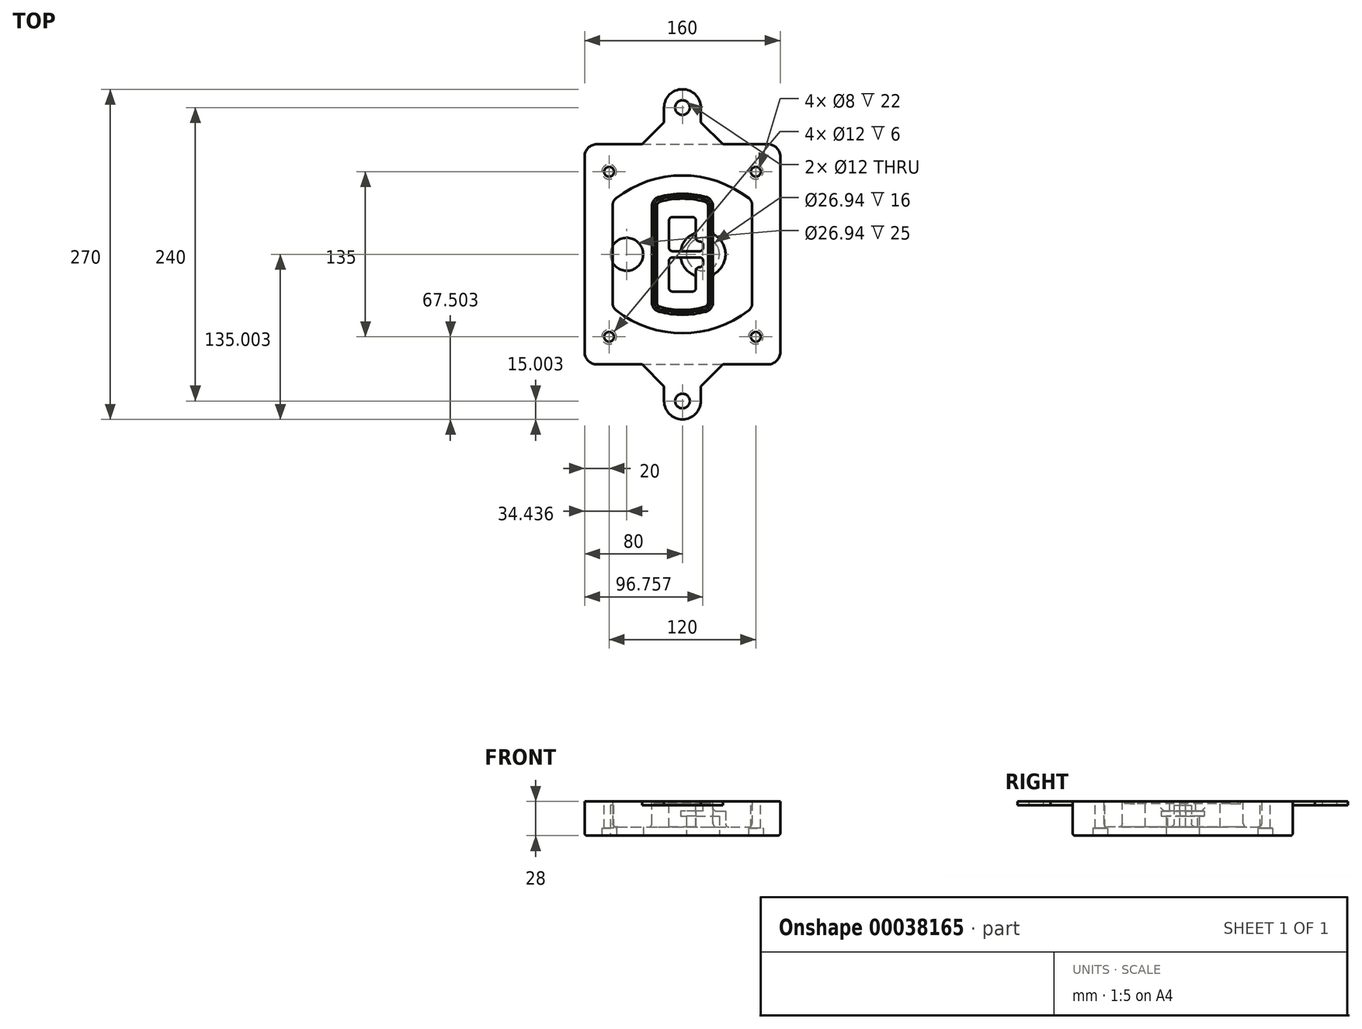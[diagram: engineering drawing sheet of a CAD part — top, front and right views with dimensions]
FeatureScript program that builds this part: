
annotation { "Feature Type Name" : "Feature", "Feature Type Description" : "" }
export const myFeature = defineFeature(function(context is Context, id is Id, definition is map)
    precondition{}
    {
        {
            var Q0;
            Q0=qCreatedBy(makeId("Top.planeOp"),FACE);
            var sketch = newSketch(context, id + "F0", { "sketchPlane" : qUnion([Q0])});
            skPoint(sketch, "E0.rect.middle", {"position": v(0, 0) * mm});
            skLineSegment(sketch, "E1.bottom", {"start": v(24.05, 28.38) * mm, "end": v(164.05, 28.38) * mm});
            skLineSegment(sketch, "E1.top", {"start": v(24.05, 208.38) * mm, "end": v(164.05, 208.38) * mm});
            skLineSegment(sketch, "E1.left", {"start": v(14.05, 38.38) * mm, "end": v(14.05, 198.38) * mm});
            skLineSegment(sketch, "E1.right", {"start": v(174.05, 38.38) * mm, "end": v(174.05, 198.38) * mm});
            skLineSegment(sketch, "E2", {"start": v(14.05, 208.38) * mm, "end": v(174.05, 28.38) * mm, "construction": true});
            skLineSegment(sketch, "E3", {"start": v(174.05, 208.38) * mm, "end": v(14.05, 28.38) * mm, "construction": true});
            skCircle(sketch, "E4", {"center": v(34.05, 185.88) * mm, "radius": 4 * mm});
            skCircle(sketch, "E5", {"center": v(154.05, 185.88) * mm, "radius": 4 * mm});
            skCircle(sketch, "E6", {"center": v(154.05, 50.88) * mm, "radius": 4 * mm});
            skCircle(sketch, "E7", {"center": v(34.05, 50.88) * mm, "radius": 4 * mm});
            skLineSegment(sketch, "E8", {"start": v(34.05, 185.88) * mm, "end": v(154.05, 185.88) * mm, "construction": true});
            skLineSegment(sketch, "E9", {"start": v(154.05, 185.88) * mm, "end": v(154.05, 50.88) * mm, "construction": true});
            skLineSegment(sketch, "E10", {"start": v(154.05, 50.88) * mm, "end": v(34.05, 50.88) * mm, "construction": true});
            skLineSegment(sketch, "E11", {"start": v(34.05, 50.88) * mm, "end": v(34.05, 185.88) * mm, "construction": true});
            skLineSegment(sketch, "E12", {"start": v(34.05, 158.68) * mm, "end": v(34.05, 78.09) * mm});
            skLineSegment(sketch, "E13", {"start": v(154.05, 158.68) * mm, "end": v(154.05, 78.09) * mm});
            skArc(sketch, "E14", {"start": v(150.2, 166.56) * mm, "mid": v(94.05, 185.88) * mm, "end": v(37.9, 166.56) * mm});
            skArc(sketch, "E15", {"start": v(37.9, 70.2) * mm, "mid": v(94.05, 50.88) * mm, "end": v(150.2, 70.2) * mm});
            skLineSegment(sketch, "E16", {"start": v(34.05, 118.38) * mm, "end": v(154.05, 118.38) * mm, "construction": true});
            skPoint(sketch, "E17.visualSharp", {"position": v(34.05, 73.38) * mm});
            skArc(sketch, "E17.filletArc", {"start": v(34.05, 78.09) * mm, "mid": v(35.06, 73.7) * mm, "end": v(37.9, 70.2) * mm});
            skPoint(sketch, "E18.visualSharp", {"position": v(34.05, 163.38) * mm});
            skArc(sketch, "E18.filletArc", {"start": v(37.9, 166.56) * mm, "mid": v(35.06, 163.06) * mm, "end": v(34.05, 158.68) * mm});
            skPoint(sketch, "E19.visualSharp", {"position": v(154.05, 163.38) * mm});
            skArc(sketch, "E19.filletArc", {"start": v(154.05, 158.68) * mm, "mid": v(153.04, 163.06) * mm, "end": v(150.2, 166.56) * mm});
            skPoint(sketch, "E20.visualSharp", {"position": v(154.05, 73.38) * mm});
            skArc(sketch, "E20.filletArc", {"start": v(150.2, 70.2) * mm, "mid": v(153.04, 73.7) * mm, "end": v(154.05, 78.09) * mm});
            skPoint(sketch, "E21.visualSharp", {"position": v(14.05, 208.38) * mm});
            skArc(sketch, "E21.filletArc", {"start": v(24.05, 208.38) * mm, "mid": v(16.98, 205.45) * mm, "end": v(14.05, 198.38) * mm});
            skPoint(sketch, "E22.visualSharp", {"position": v(174.05, 208.38) * mm});
            skArc(sketch, "E22.filletArc", {"start": v(174.05, 198.38) * mm, "mid": v(171.12, 205.45) * mm, "end": v(164.05, 208.38) * mm});
            skPoint(sketch, "E23.visualSharp", {"position": v(174.05, 28.38) * mm});
            skArc(sketch, "E23.filletArc", {"start": v(164.05, 28.38) * mm, "mid": v(171.12, 31.31) * mm, "end": v(174.05, 38.38) * mm});
            skPoint(sketch, "E24.visualSharp", {"position": v(14.05, 28.38) * mm});
            skArc(sketch, "E24.filletArc", {"start": v(14.05, 38.38) * mm, "mid": v(16.98, 31.31) * mm, "end": v(24.05, 28.38) * mm});
            skArc(sketch, "E25.0", {"start": v(151.05, 158.68) * mm, "mid": v(150.34, 161.75) * mm, "end": v(148.36, 164.2) * mm});
            skLineSegment(sketch, "E25.1", {"start": v(151.05, 158.68) * mm, "end": v(151.05, 78.09) * mm});
            skArc(sketch, "E25.2", {"start": v(148.36, 72.57) * mm, "mid": v(150.34, 75.02) * mm, "end": v(151.05, 78.09) * mm});
            skArc(sketch, "E25.3", {"start": v(39.74, 72.57) * mm, "mid": v(94.05, 53.88) * mm, "end": v(148.36, 72.57) * mm});
            skArc(sketch, "E25.4", {"start": v(37.05, 78.09) * mm, "mid": v(37.76, 75.02) * mm, "end": v(39.74, 72.57) * mm});
            skArc(sketch, "E25.5", {"start": v(148.36, 164.2) * mm, "mid": v(94.05, 182.88) * mm, "end": v(39.74, 164.2) * mm});
            skLineSegment(sketch, "E25.6", {"start": v(37.05, 158.68) * mm, "end": v(37.05, 78.09) * mm});
            skArc(sketch, "E25.7", {"start": v(39.74, 164.2) * mm, "mid": v(37.76, 161.75) * mm, "end": v(37.05, 158.68) * mm});
            skArc(sketch, "E26.0", {"start": v(35.43, 169.71) * mm, "mid": v(31.47, 164.82) * mm, "end": v(30.05, 158.68) * mm});
            skArc(sketch, "E26.1", {"start": v(152.67, 169.71) * mm, "mid": v(94.05, 189.88) * mm, "end": v(35.43, 169.71) * mm});
            skArc(sketch, "E26.2", {"start": v(158.05, 158.68) * mm, "mid": v(156.63, 164.82) * mm, "end": v(152.67, 169.71) * mm});
            skLineSegment(sketch, "E26.3", {"start": v(158.05, 158.68) * mm, "end": v(158.05, 78.09) * mm});
            skArc(sketch, "E26.4", {"start": v(152.67, 67.05) * mm, "mid": v(156.63, 71.95) * mm, "end": v(158.05, 78.09) * mm});
            skLineSegment(sketch, "E26.5", {"start": v(30.05, 158.68) * mm, "end": v(30.05, 78.09) * mm});
            skArc(sketch, "E26.6", {"start": v(35.43, 67.05) * mm, "mid": v(94.05, 46.88) * mm, "end": v(152.67, 67.05) * mm});
            skArc(sketch, "E26.7", {"start": v(30.05, 78.09) * mm, "mid": v(31.47, 71.95) * mm, "end": v(35.43, 67.05) * mm});
            skSolve(sketch);
        }
        {
            var Q0;
            Q0=makeQuery(id+"F0.imprint","IMPRINT",FACE,{"disambiguationData":[TD([[makeQuery(id+"F0.imprint","IMPRINT",EDGE,{"derivedFrom":sQuery(id+"F0.wireOp",EDGE,"E1.bottom")}),1.0]])]});
            var Q1;
            Q1=makeQuery(id+"F0.imprint","IMPRINT",FACE,{"disambiguationData":[TD([[makeQuery(id+"F0.imprint","IMPRINT",EDGE,{"derivedFrom":sQuery(id+"F0.wireOp",EDGE,"E12")}),1.0]])]});
            var Q2;
            Q2=makeQuery(id+"F0.imprint","IMPRINT",FACE,{"disambiguationData":[TD([[makeQuery(id+"F0.imprint","IMPRINT",EDGE,{"derivedFrom":sQuery(id+"F0.wireOp",EDGE,"E25.0")}),1.0]])]});
            var Q3;
            Q3=makeQuery(id+"F0.imprint","IMPRINT",FACE,{"disambiguationData":[TD([[makeQuery(id+"F0.imprint","IMPRINT",EDGE,{"derivedFrom":sQuery(id+"F0.wireOp",EDGE,"E12")}),-1.0]])]});
            extrude(context, id + "F1", {"entities" : qUnion([Q0, Q1, Q2, Q3]), "oppositeDirection" : true, "depth" : 25 * mm});
        }
        {
            var Q0;
            Q0=makeQuery(id+"F0.imprint","IMPRINT",FACE,{"disambiguationData":[TD([[makeQuery(id+"F0.imprint","IMPRINT",EDGE,{"derivedFrom":sQuery(id+"F0.wireOp",EDGE,"E12")}),1.0]])]});
            extrude(context, id + "F2", {"entities" : qUnion([Q0]), "operationType" : NewBodyOperationType.ADD, "depth" : 3 * mm});
        }
        {
            var Q0;
            Q0=makeQuery(id+"F0.imprint","IMPRINT",FACE,{"disambiguationData":[TD([[makeQuery(id+"F0.imprint","IMPRINT",EDGE,{"derivedFrom":sQuery(id+"F0.wireOp",EDGE,"E25.0")}),1.0]])]});
            extrude(context, id + "F3", {"entities" : qUnion([Q0]), "operationType" : NewBodyOperationType.REMOVE, "oppositeDirection" : true, "depth" : 18 * mm});
        }
        {
            var Q0;
            Q0=makeQuery(id+"F2.opExtrude","CAP_FACE",FACE,{"disambiguationData":[OSD([sQuery(id+"F0.wireOp",EDGE,"E12"),sQuery(id+"F0.wireOp",EDGE,"E13"),sQuery(id+"F0.wireOp",EDGE,"E14"),sQuery(id+"F0.wireOp",EDGE,"E15"),sQuery(id+"F0.wireOp",EDGE,"E17.filletArc"),sQuery(id+"F0.wireOp",EDGE,"E18.filletArc"),sQuery(id+"F0.wireOp",EDGE,"E19.filletArc"),sQuery(id+"F0.wireOp",EDGE,"E20.filletArc"),sQuery(id+"F0.wireOp",EDGE,"E25.0"),sQuery(id+"F0.wireOp",EDGE,"E25.1"),sQuery(id+"F0.wireOp",EDGE,"E25.2"),sQuery(id+"F0.wireOp",EDGE,"E25.3"),sQuery(id+"F0.wireOp",EDGE,"E25.4"),sQuery(id+"F0.wireOp",EDGE,"E25.5"),sQuery(id+"F0.wireOp",EDGE,"E25.6"),sQuery(id+"F0.wireOp",EDGE,"E25.7")])],"isStart":false});
            var sketch = newSketch(context, id + "F4", { "sketchPlane" : qUnion([Q0])});
            skArc(sketch, "E27.0", {"start": v(74.97, 71.41) * mm, "mid": v(94.05, 68.88) * mm, "end": v(113.13, 71.41) * mm});
            skArc(sketch, "E28.0", {"start": v(113.13, 165.35) * mm, "mid": v(94.05, 167.88) * mm, "end": v(74.97, 165.35) * mm});
            skLineSegment(sketch, "E29", {"start": v(69.05, 157.63) * mm, "end": v(69.05, 79.14) * mm});
            skLineSegment(sketch, "E30", {"start": v(119.05, 157.63) * mm, "end": v(119.05, 79.14) * mm});
            skLineSegment(sketch, "E31", {"start": v(69.05, 163.48) * mm, "end": v(119.05, 163.48) * mm, "construction": true});
            skLineSegment(sketch, "E32", {"start": v(69.05, 73.28) * mm, "end": v(119.05, 73.28) * mm, "construction": true});
            skPoint(sketch, "E33.visualSharp", {"position": v(69.05, 163.48) * mm});
            skArc(sketch, "E33.filletArc", {"start": v(74.97, 165.35) * mm, "mid": v(70.7, 162.5) * mm, "end": v(69.05, 157.63) * mm});
            skPoint(sketch, "E34.visualSharp", {"position": v(119.05, 163.48) * mm});
            skArc(sketch, "E34.filletArc", {"start": v(119.05, 157.63) * mm, "mid": v(117.4, 162.5) * mm, "end": v(113.13, 165.35) * mm});
            skPoint(sketch, "E35.visualSharp", {"position": v(119.05, 73.28) * mm});
            skArc(sketch, "E35.filletArc", {"start": v(113.13, 71.41) * mm, "mid": v(117.4, 74.27) * mm, "end": v(119.05, 79.14) * mm});
            skPoint(sketch, "E36.visualSharp", {"position": v(69.05, 73.28) * mm});
            skArc(sketch, "E36.filletArc", {"start": v(69.05, 79.14) * mm, "mid": v(70.7, 74.27) * mm, "end": v(74.97, 71.41) * mm});
            skArc(sketch, "E37.0", {"start": v(148.36, 164.2) * mm, "mid": v(94.05, 182.88) * mm, "end": v(39.74, 164.2) * mm});
            skArc(sketch, "E37.1", {"start": v(39.74, 164.2) * mm, "mid": v(37.76, 161.75) * mm, "end": v(37.05, 158.68) * mm});
            skLineSegment(sketch, "E37.2", {"start": v(37.05, 158.68) * mm, "end": v(37.05, 78.09) * mm});
            skArc(sketch, "E37.3", {"start": v(37.05, 78.09) * mm, "mid": v(37.76, 75.02) * mm, "end": v(39.74, 72.57) * mm});
            skArc(sketch, "E37.4", {"start": v(39.74, 72.57) * mm, "mid": v(94.05, 53.88) * mm, "end": v(148.36, 72.57) * mm});
            skArc(sketch, "E37.5", {"start": v(148.36, 72.57) * mm, "mid": v(150.34, 75.02) * mm, "end": v(151.05, 78.09) * mm});
            skLineSegment(sketch, "E37.6", {"start": v(151.05, 158.68) * mm, "end": v(151.05, 78.09) * mm});
            skArc(sketch, "E37.7", {"start": v(151.05, 158.68) * mm, "mid": v(150.34, 161.75) * mm, "end": v(148.36, 164.2) * mm});
            skLineSegment(sketch, "E38.0", {"start": v(117.05, 157.63) * mm, "end": v(117.05, 79.14) * mm});
            skArc(sketch, "E38.1", {"start": v(112.61, 73.34) * mm, "mid": v(115.81, 75.49) * mm, "end": v(117.05, 79.14) * mm});
            skArc(sketch, "E38.2", {"start": v(75.49, 73.34) * mm, "mid": v(94.05, 70.88) * mm, "end": v(112.61, 73.34) * mm});
            skArc(sketch, "E38.3", {"start": v(71.05, 79.14) * mm, "mid": v(72.29, 75.49) * mm, "end": v(75.49, 73.34) * mm});
            skLineSegment(sketch, "E38.4", {"start": v(71.05, 157.63) * mm, "end": v(71.05, 79.14) * mm});
            skArc(sketch, "E38.5", {"start": v(117.05, 157.63) * mm, "mid": v(115.81, 161.28) * mm, "end": v(112.61, 163.42) * mm});
            skArc(sketch, "E38.6", {"start": v(75.49, 163.42) * mm, "mid": v(72.29, 161.28) * mm, "end": v(71.05, 157.63) * mm});
            skArc(sketch, "E38.7", {"start": v(112.61, 163.42) * mm, "mid": v(94.05, 165.88) * mm, "end": v(75.49, 163.42) * mm});
            skArc(sketch, "E39.0", {"start": v(115.05, 157.63) * mm, "mid": v(114.23, 160.06) * mm, "end": v(112.1, 161.5) * mm});
            skLineSegment(sketch, "E39.1", {"start": v(115.05, 157.63) * mm, "end": v(115.05, 79.14) * mm});
            skArc(sketch, "E39.2", {"start": v(112.1, 75.27) * mm, "mid": v(114.23, 76.7) * mm, "end": v(115.05, 79.14) * mm});
            skArc(sketch, "E39.3", {"start": v(76, 75.27) * mm, "mid": v(94.05, 72.88) * mm, "end": v(112.1, 75.27) * mm});
            skArc(sketch, "E39.4", {"start": v(73.05, 79.14) * mm, "mid": v(73.87, 76.7) * mm, "end": v(76, 75.27) * mm});
            skArc(sketch, "E39.5", {"start": v(112.1, 161.5) * mm, "mid": v(94.05, 163.88) * mm, "end": v(76, 161.5) * mm});
            skLineSegment(sketch, "E39.6", {"start": v(73.05, 157.63) * mm, "end": v(73.05, 79.14) * mm});
            skArc(sketch, "E39.7", {"start": v(76, 161.5) * mm, "mid": v(73.87, 160.06) * mm, "end": v(73.05, 157.63) * mm});
            skLineSegment(sketch, "E40", {"start": v(69.05, 118.38) * mm, "end": v(119.05, 118.38) * mm, "construction": true});
            skLineSegment(sketch, "E41", {"start": v(83.05, 123.88) * mm, "end": v(83.05, 145.88) * mm});
            skLineSegment(sketch, "E42", {"start": v(86.05, 148.88) * mm, "end": v(102.05, 148.88) * mm});
            skLineSegment(sketch, "E43", {"start": v(105.05, 145.88) * mm, "end": v(105.05, 131.88) * mm});
            skLineSegment(sketch, "E44", {"start": v(108.05, 128.88) * mm, "end": v(108.05, 128.88) * mm});
            skLineSegment(sketch, "E45", {"start": v(111.05, 125.88) * mm, "end": v(111.05, 123.88) * mm});
            skLineSegment(sketch, "E46", {"start": v(108.05, 120.88) * mm, "end": v(86.05, 120.88) * mm});
            skPoint(sketch, "E47.visualSharp", {"position": v(83.05, 148.88) * mm});
            skArc(sketch, "E47.filletArc", {"start": v(86.05, 148.88) * mm, "mid": v(83.93, 148) * mm, "end": v(83.05, 145.88) * mm});
            skPoint(sketch, "E48.visualSharp", {"position": v(105.05, 148.88) * mm});
            skArc(sketch, "E48.filletArc", {"start": v(105.05, 145.88) * mm, "mid": v(104.17, 148) * mm, "end": v(102.05, 148.88) * mm});
            skPoint(sketch, "E49.visualSharp", {"position": v(105.05, 128.88) * mm});
            skArc(sketch, "E49.filletArc", {"start": v(105.05, 131.88) * mm, "mid": v(105.93, 129.76) * mm, "end": v(108.05, 128.88) * mm});
            skPoint(sketch, "E50.visualSharp", {"position": v(111.05, 128.88) * mm});
            skArc(sketch, "E50.filletArc", {"start": v(111.05, 125.88) * mm, "mid": v(110.17, 128) * mm, "end": v(108.05, 128.88) * mm});
            skPoint(sketch, "E51.visualSharp", {"position": v(111.05, 120.88) * mm});
            skArc(sketch, "E51.filletArc", {"start": v(108.05, 120.88) * mm, "mid": v(110.17, 121.76) * mm, "end": v(111.05, 123.88) * mm});
            skPoint(sketch, "E52.visualSharp", {"position": v(83.05, 120.88) * mm});
            skArc(sketch, "E52.filletArc", {"start": v(83.05, 123.88) * mm, "mid": v(83.93, 121.76) * mm, "end": v(86.05, 120.88) * mm});
            skLineSegment(sketch, "E53.0.MirrorCS", {"start": v(108.05, 115.88) * mm, "end": v(86.05, 115.88) * mm});
            skArc(sketch, "E54.0.MirrorCS", {"start": v(83.05, 112.88) * mm, "mid": v(83.93, 115) * mm, "end": v(86.05, 115.88) * mm});
            skLineSegment(sketch, "E55.0.MirrorCS", {"start": v(83.05, 112.88) * mm, "end": v(83.05, 90.88) * mm});
            skArc(sketch, "E56.0.MirrorCS", {"start": v(86.05, 87.88) * mm, "mid": v(83.93, 88.76) * mm, "end": v(83.05, 90.88) * mm});
            skLineSegment(sketch, "E57.0.MirrorCS", {"start": v(86.05, 87.88) * mm, "end": v(102.05, 87.88) * mm});
            skArc(sketch, "E58.0.MirrorCS", {"start": v(105.05, 90.88) * mm, "mid": v(104.17, 88.76) * mm, "end": v(102.05, 87.88) * mm});
            skLineSegment(sketch, "E59.0.MirrorCS", {"start": v(105.05, 90.88) * mm, "end": v(105.05, 104.88) * mm});
            skArc(sketch, "E60.0.MirrorCS", {"start": v(105.05, 104.88) * mm, "mid": v(105.93, 107) * mm, "end": v(108.05, 107.88) * mm});
            skArc(sketch, "E61.0.MirrorCS", {"start": v(111.05, 110.88) * mm, "mid": v(110.17, 108.76) * mm, "end": v(108.05, 107.88) * mm});
            skLineSegment(sketch, "E62.0.MirrorCS", {"start": v(111.05, 110.88) * mm, "end": v(111.05, 112.88) * mm});
            skArc(sketch, "E63.0.MirrorCS", {"start": v(108.05, 115.88) * mm, "mid": v(110.17, 115) * mm, "end": v(111.05, 112.88) * mm});
            skSolve(sketch);
        }
        {
            var Q0;
            Q0=makeQuery(id+"F4.imprint","IMPRINT",FACE,{"disambiguationData":[TD([[makeQuery(id+"F4.imprint","IMPRINT",EDGE,{"derivedFrom":sQuery(id+"F4.wireOp",EDGE,"E27.0")}),1.0]])]});
            var Q1;
            Q1=makeQuery(id+"F4.imprint","IMPRINT",FACE,{"disambiguationData":[TD([[makeQuery(id+"F4.imprint","IMPRINT",EDGE,{"derivedFrom":sQuery(id+"F4.wireOp",EDGE,"E38.0")}),-1.0]])]});
            var Q2;
            Q2=makeQuery(id+"F4.imprint","IMPRINT",FACE,{"disambiguationData":[TD([[makeQuery(id+"F4.imprint","IMPRINT",EDGE,{"derivedFrom":sQuery(id+"F4.wireOp",EDGE,"E39.0")}),1.0]])]});
            extrude(context, id + "F5", {"entities" : qUnion([Q0, Q1, Q2]), "operationType" : NewBodyOperationType.ADD, "endBound" : BoundingType.UP_TO_NEXT, "oppositeDirection" : true, "depth" : 25 * mm});
        }
        {
            var Q0;
            Q0=makeQuery(id+"F4.imprint","IMPRINT",FACE,{"disambiguationData":[TD([[makeQuery(id+"F4.imprint","IMPRINT",EDGE,{"derivedFrom":sQuery(id+"F4.wireOp",EDGE,"E38.0")}),-1.0]])]});
            extrude(context, id + "F6", {"entities" : qUnion([Q0]), "operationType" : NewBodyOperationType.REMOVE, "oppositeDirection" : true, "depth" : 2 * mm});
        }
        {
            var Q0;
            Q0=makeQuery(id+"F1.opExtrude","CAP_FACE",FACE,{"disambiguationData":[OSD([sQuery(id+"F0.wireOp",EDGE,"E1.bottom"),sQuery(id+"F0.wireOp",EDGE,"E1.top"),sQuery(id+"F0.wireOp",EDGE,"E1.left"),sQuery(id+"F0.wireOp",EDGE,"E1.right"),sQuery(id+"F0.wireOp",EDGE,"E4"),sQuery(id+"F0.wireOp",EDGE,"E5"),sQuery(id+"F0.wireOp",EDGE,"E6"),sQuery(id+"F0.wireOp",EDGE,"E7"),sQuery(id+"F0.wireOp",EDGE,"E21.filletArc"),sQuery(id+"F0.wireOp",EDGE,"E22.filletArc"),sQuery(id+"F0.wireOp",EDGE,"E23.filletArc"),sQuery(id+"F0.wireOp",EDGE,"E24.filletArc")])],"isStart":false});
            var sketch = newSketch(context, id + "F7", { "sketchPlane" : qUnion([Q0])});
            skCircle(sketch, "E64", {"center": v(110.8, -118.38) * mm, "radius": 13.47 * mm});
            skCircle(sketch, "E65", {"center": v(48.49, -118.38) * mm, "radius": 13.47 * mm});
            skLineSegment(sketch, "E66", {"start": v(174.05, -118.38) * mm, "end": v(14.05, -118.38) * mm});
            skCircle(sketch, "E67", {"center": v(110.8, -118.38) * mm, "radius": 18.47 * mm});
            skCircle(sketch, "E68", {"center": v(154.05, -185.88) * mm, "radius": 6 * mm});
            skCircle(sketch, "E69", {"center": v(34.05, -185.88) * mm, "radius": 6 * mm});
            skCircle(sketch, "E70", {"center": v(34.05, -50.88) * mm, "radius": 6 * mm});
            skCircle(sketch, "E71", {"center": v(154.05, -50.88) * mm, "radius": 6 * mm});
            skSolve(sketch);
        }
        {
            var Q0;
            {var subQ1=sQuery(id+"F7.wireOp",EDGE,"E66");var subQ4=sQuery(id+"F7.wireOp",EDGE,"E64");var subQ6=makeQuery(id+"F7.imprint","INTERSECT",VERTEX,{"disambiguationData":[OD(0.0)],"derivedFrom":[subQ4,subQ1]});Q0=makeQuery(id+"F7.imprint","IMPRINT",FACE,{"disambiguationData":[TD([[makeQuery(id+"F7.imprint","IMPRINT",EDGE,{"disambiguationData":[TD([[subQ6,-1.0]])],"derivedFrom":subQ4}),-1.0]])]});}
            var Q1;
            {var subQ0=sQuery(id+"F7.wireOp",EDGE,"E66");var subQ1=sQuery(id+"F7.wireOp",EDGE,"E64");var subQ3=makeQuery(id+"F7.imprint","INTERSECT",VERTEX,{"disambiguationData":[OD(0.0)],"derivedFrom":[subQ1,subQ0]});Q1=makeQuery(id+"F7.imprint","IMPRINT",FACE,{"disambiguationData":[TD([[makeQuery(id+"F7.imprint","IMPRINT",EDGE,{"disambiguationData":[TD([[subQ3,-1.0]])],"derivedFrom":subQ1}),1.0]])]});}
            var Q2;
            {var subQ0=sQuery(id+"F7.wireOp",EDGE,"E66");var subQ1=sQuery(id+"F7.wireOp",EDGE,"E64");var subQ3=makeQuery(id+"F7.imprint","INTERSECT",VERTEX,{"disambiguationData":[OD(0.0)],"derivedFrom":[subQ1,subQ0]});Q2=makeQuery(id+"F7.imprint","IMPRINT",FACE,{"disambiguationData":[TD([[makeQuery(id+"F7.imprint","IMPRINT",EDGE,{"disambiguationData":[TD([[subQ3,1.0]])],"derivedFrom":subQ1}),1.0]])]});}
            var Q3;
            {var subQ1=sQuery(id+"F7.wireOp",EDGE,"E66");var subQ4=sQuery(id+"F7.wireOp",EDGE,"E64");var subQ6=makeQuery(id+"F7.imprint","INTERSECT",VERTEX,{"disambiguationData":[OD(0.0)],"derivedFrom":[subQ4,subQ1]});Q3=makeQuery(id+"F7.imprint","IMPRINT",FACE,{"disambiguationData":[TD([[makeQuery(id+"F7.imprint","IMPRINT",EDGE,{"disambiguationData":[TD([[subQ6,1.0]])],"derivedFrom":subQ4}),-1.0]])]});}
            extrude(context, id + "F8", {"entities" : qUnion([Q0, Q1, Q2, Q3]), "operationType" : NewBodyOperationType.ADD, "oppositeDirection" : true, "depth" : 20 * mm});
        }
        {
            var Q0;
            {var subQ0=sQuery(id+"F7.wireOp",EDGE,"E66");var subQ1=sQuery(id+"F7.wireOp",EDGE,"E64");var subQ3=makeQuery(id+"F7.imprint","INTERSECT",VERTEX,{"disambiguationData":[OD(0.0)],"derivedFrom":[subQ1,subQ0]});Q0=makeQuery(id+"F7.imprint","IMPRINT",FACE,{"disambiguationData":[TD([[makeQuery(id+"F7.imprint","IMPRINT",EDGE,{"disambiguationData":[TD([[subQ3,-1.0]])],"derivedFrom":subQ1}),1.0]])]});}
            var Q1;
            {var subQ0=sQuery(id+"F7.wireOp",EDGE,"E66");var subQ1=sQuery(id+"F7.wireOp",EDGE,"E64");var subQ3=makeQuery(id+"F7.imprint","INTERSECT",VERTEX,{"disambiguationData":[OD(0.0)],"derivedFrom":[subQ1,subQ0]});Q1=makeQuery(id+"F7.imprint","IMPRINT",FACE,{"disambiguationData":[TD([[makeQuery(id+"F7.imprint","IMPRINT",EDGE,{"disambiguationData":[TD([[subQ3,1.0]])],"derivedFrom":subQ1}),1.0]])]});}
            extrude(context, id + "F9", {"entities" : qUnion([Q0, Q1]), "operationType" : NewBodyOperationType.REMOVE, "oppositeDirection" : true, "depth" : 16 * mm});
        }
        {
            var Q0;
            {var subQ0=sQuery(id+"F7.wireOp",EDGE,"E66");var subQ1=sQuery(id+"F7.wireOp",EDGE,"E65");var subQ3=makeQuery(id+"F7.imprint","INTERSECT",VERTEX,{"disambiguationData":[OD(0.0)],"derivedFrom":[subQ1,subQ0]});Q0=makeQuery(id+"F7.imprint","IMPRINT",FACE,{"disambiguationData":[TD([[makeQuery(id+"F7.imprint","IMPRINT",EDGE,{"disambiguationData":[TD([[subQ3,-1.0]])],"derivedFrom":subQ1}),1.0]])]});}
            var Q1;
            {var subQ0=sQuery(id+"F7.wireOp",EDGE,"E66");var subQ1=sQuery(id+"F7.wireOp",EDGE,"E65");var subQ3=makeQuery(id+"F7.imprint","INTERSECT",VERTEX,{"disambiguationData":[OD(0.0)],"derivedFrom":[subQ1,subQ0]});Q1=makeQuery(id+"F7.imprint","IMPRINT",FACE,{"disambiguationData":[TD([[makeQuery(id+"F7.imprint","IMPRINT",EDGE,{"disambiguationData":[TD([[subQ3,1.0]])],"derivedFrom":subQ1}),1.0]])]});}
            extrude(context, id + "F10", {"entities" : qUnion([Q0, Q1]), "operationType" : NewBodyOperationType.REMOVE, "oppositeDirection" : true, "depth" : 25 * mm});
        }
        {
            var Q0;
            Q0=makeQuery(id+"F7.imprint","IMPRINT",FACE,{"disambiguationData":[TD([[makeQuery(id+"F7.imprint","IMPRINT",EDGE,{"derivedFrom":sQuery(id+"F7.wireOp",EDGE,"E68")}),1.0]])]});
            var Q1;
            Q1=makeQuery(id+"F7.imprint","IMPRINT",FACE,{"disambiguationData":[TD([[makeQuery(id+"F7.imprint","IMPRINT",EDGE,{"derivedFrom":makeQuery(id+"F1.opExtrude","CAP_EDGE",EDGE,{"disambiguationData":[OSD([sQuery(id+"F0.wireOp",EDGE,"E5")])],"isStart":false})}),-1.0]])]});
            var Q2;
            Q2=makeQuery(id+"F7.imprint","IMPRINT",FACE,{"disambiguationData":[TD([[makeQuery(id+"F7.imprint","IMPRINT",EDGE,{"derivedFrom":sQuery(id+"F7.wireOp",EDGE,"E69")}),1.0]])]});
            var Q3;
            Q3=makeQuery(id+"F7.imprint","IMPRINT",FACE,{"disambiguationData":[TD([[makeQuery(id+"F7.imprint","IMPRINT",EDGE,{"derivedFrom":makeQuery(id+"F1.opExtrude","CAP_EDGE",EDGE,{"disambiguationData":[OSD([sQuery(id+"F0.wireOp",EDGE,"E4")])],"isStart":false})}),-1.0]])]});
            var Q4;
            Q4=makeQuery(id+"F7.imprint","IMPRINT",FACE,{"disambiguationData":[TD([[makeQuery(id+"F7.imprint","IMPRINT",EDGE,{"derivedFrom":sQuery(id+"F7.wireOp",EDGE,"E70")}),1.0]])]});
            var Q5;
            Q5=makeQuery(id+"F7.imprint","IMPRINT",FACE,{"disambiguationData":[TD([[makeQuery(id+"F7.imprint","IMPRINT",EDGE,{"derivedFrom":makeQuery(id+"F1.opExtrude","CAP_EDGE",EDGE,{"disambiguationData":[OSD([sQuery(id+"F0.wireOp",EDGE,"E7")])],"isStart":false})}),-1.0]])]});
            var Q6;
            Q6=makeQuery(id+"F7.imprint","IMPRINT",FACE,{"disambiguationData":[TD([[makeQuery(id+"F7.imprint","IMPRINT",EDGE,{"derivedFrom":sQuery(id+"F7.wireOp",EDGE,"E71")}),1.0]])]});
            var Q7;
            Q7=makeQuery(id+"F7.imprint","IMPRINT",FACE,{"disambiguationData":[TD([[makeQuery(id+"F7.imprint","IMPRINT",EDGE,{"derivedFrom":makeQuery(id+"F1.opExtrude","CAP_EDGE",EDGE,{"disambiguationData":[OSD([sQuery(id+"F0.wireOp",EDGE,"E6")])],"isStart":false})}),-1.0]])]});
            extrude(context, id + "F11", {"entities" : qUnion([Q0, Q1, Q2, Q3, Q4, Q5, Q6, Q7]), "operationType" : NewBodyOperationType.REMOVE, "oppositeDirection" : true, "depth" : 6 * mm});
        }
        {
            var Q0;
            Q0=makeQuery(id+"F9.boolean.opBoolean","COPY",FACE,{"derivedFrom":makeQuery(id+"F9.opExtrude","CAP_FACE",FACE,{"disambiguationData":[OSD([sQuery(id+"F7.wireOp",EDGE,"E64")])],"isStart":false})});
            var sketch = newSketch(context, id + "F12", { "sketchPlane" : qUnion([Q0])});
            skArc(sketch, "E72.0", {"start": v(105.05, -100.83) * mm, "mid": v(96.62, -106.56) * mm, "end": v(92.5, -115.88) * mm});
            skArc(sketch, "E72.1", {"start": v(92.5, -120.88) * mm, "mid": v(96.62, -130.2) * mm, "end": v(105.05, -135.93) * mm});
            skLineSegment(sketch, "E73", {"start": v(92.5, -120.88) * mm, "end": v(108.05, -120.88) * mm});
            skLineSegment(sketch, "E74.0", {"start": v(108.05, -115.88) * mm, "end": v(92.5, -115.88) * mm});
            skArc(sketch, "E74.1", {"start": v(108.05, -115.88) * mm, "mid": v(110.17, -115) * mm, "end": v(111.05, -112.88) * mm});
            skLineSegment(sketch, "E74.2", {"start": v(111.05, -110.88) * mm, "end": v(111.05, -112.88) * mm});
            skArc(sketch, "E74.3", {"start": v(111.05, -110.88) * mm, "mid": v(110.17, -108.76) * mm, "end": v(108.05, -107.88) * mm});
            skArc(sketch, "E74.4", {"start": v(105.05, -104.88) * mm, "mid": v(105.93, -107) * mm, "end": v(108.05, -107.88) * mm});
            skLineSegment(sketch, "E74.5", {"start": v(105.05, -100.83) * mm, "end": v(105.05, -104.88) * mm});
            skLineSegment(sketch, "E74.7", {"start": v(108.05, -120.88) * mm, "end": v(92.5, -120.88) * mm});
            skArc(sketch, "E74.8", {"start": v(108.05, -120.88) * mm, "mid": v(110.17, -121.76) * mm, "end": v(111.05, -123.88) * mm});
            skLineSegment(sketch, "E74.9", {"start": v(111.05, -125.88) * mm, "end": v(111.05, -123.88) * mm});
            skArc(sketch, "E74.10", {"start": v(111.05, -125.88) * mm, "mid": v(110.17, -128) * mm, "end": v(108.05, -128.88) * mm});
            skArc(sketch, "E74.11", {"start": v(105.05, -131.88) * mm, "mid": v(105.93, -129.76) * mm, "end": v(108.05, -128.88) * mm});
            skLineSegment(sketch, "E74.12", {"start": v(105.05, -135.93) * mm, "end": v(105.05, -131.88) * mm});
            skPoint(sketch, "E75.orphan", {"position": v(105.05, -145.88) * mm});
            skPoint(sketch, "E76.orphan", {"position": v(86.05, -120.88) * mm});
            skPoint(sketch, "E77.orphan", {"position": v(86.05, -115.88) * mm});
            skPoint(sketch, "E78.orphan", {"position": v(105.05, -90.88) * mm});
            skSolve(sketch);
        }
        {
            var Q0;
            {var subQ7=sQuery(id+"F12.wireOp",EDGE,"E72.0");var subQ14=sQuery(id+"F12.wireOp",EDGE,"E72.1");var subQ16=sQuery(id+"F12.wireOp",EDGE,"E74.1");var subQ18=sQuery(id+"F12.wireOp",EDGE,"E74.8");Q0=qUnion([makeQuery(id+"F12.imprint","IMPRINT",FACE,{"disambiguationData":[TD([[makeQuery(id+"F12.imprint","IMPRINT",EDGE,{"derivedFrom":subQ7}),1.0]])]}),makeQuery(id+"F12.imprint","IMPRINT",FACE,{"disambiguationData":[TD([[makeQuery(id+"F12.imprint","IMPRINT",EDGE,{"derivedFrom":subQ14}),1.0]])]}),makeQuery(id+"F12.imprint","IMPRINT",FACE,{"disambiguationData":[TD([[makeQuery(id+"F12.imprint","IMPRINT",EDGE,{"derivedFrom":subQ16}),1.0]])]}),makeQuery(id+"F12.imprint","IMPRINT",FACE,{"disambiguationData":[TD([[makeQuery(id+"F12.imprint","IMPRINT",EDGE,{"derivedFrom":subQ18}),-1.0]])]})]);}
            var Q1;
            Q1=makeQuery(id+"F5.boolean.opBoolean","SPLIT",FACE,{"disambiguationData":[TD([makeQuery(id+"F5.opExtrude","SWEPT_FACE",FACE,{"disambiguationData":[OSD([sQuery(id+"F4.wireOp",EDGE,"E41")])]})])],"derivedFrom":makeQuery(id+"F3.boolean.opBoolean","COPY",FACE,{"derivedFrom":makeQuery(id+"F3.opExtrude","CAP_FACE",FACE,{"disambiguationData":[OSD([sQuery(id+"F0.wireOp",EDGE,"E25.0"),sQuery(id+"F0.wireOp",EDGE,"E25.1"),sQuery(id+"F0.wireOp",EDGE,"E25.2"),sQuery(id+"F0.wireOp",EDGE,"E25.3"),sQuery(id+"F0.wireOp",EDGE,"E25.4"),sQuery(id+"F0.wireOp",EDGE,"E25.5"),sQuery(id+"F0.wireOp",EDGE,"E25.6"),sQuery(id+"F0.wireOp",EDGE,"E25.7")])],"isStart":false})})});
            extrude(context, id + "F13", {"entities" : qUnion([Q0]), "operationType" : NewBodyOperationType.REMOVE, "endBound" : BoundingType.UP_TO_SURFACE, "endBoundEntityFace" : qUnion([Q1]), "depth" : 25 * mm});
        }
        {
            var Q0;
            Q0=makeQuery(id+"F3.boolean.opBoolean","COPY",EDGE,{"derivedFrom":makeQuery(id+"F3.opExtrude","CAP_EDGE",EDGE,{"disambiguationData":[OSD([sQuery(id+"F0.wireOp",EDGE,"E25.6")])],"isStart":false})});
            var Q1;
            Q1=makeQuery(id+"F8.boolean.opBoolean","INTERSECT",EDGE,{"derivedFrom":[makeQuery(id+"F5.opExtrude","SWEPT_FACE",FACE,{"disambiguationData":[OSD([sQuery(id+"F4.wireOp",EDGE,"E30")])]}),makeQuery(id+"F8.opExtrude","CAP_FACE",FACE,{"disambiguationData":[OSD([sQuery(id+"F7.wireOp",EDGE,"E67")])],"isStart":false})]});
            var Q2;
            Q2=makeQuery(id+"F8.boolean.opBoolean","INTERSECT",EDGE,{"disambiguationData":[OD(1.0)],"derivedFrom":[makeQuery(id+"F5.opExtrude","SWEPT_FACE",FACE,{"disambiguationData":[OSD([sQuery(id+"F4.wireOp",EDGE,"E30")])]}),makeQuery(id+"F8.opExtrude","SWEPT_FACE",FACE,{"disambiguationData":[OSD([sQuery(id+"F7.wireOp",EDGE,"E67")])]})]});
            var Q3;
            {var subQ0=sQuery(id+"F4.wireOp",EDGE,"E30");Q3=makeQuery(id+"F8.boolean.opBoolean","SPLIT",EDGE,{"disambiguationData":[TD([makeQuery(id+"F5.opExtrude","SWEPT_FACE",FACE,{"disambiguationData":[OSD([sQuery(id+"F4.wireOp",EDGE,"E35.filletArc")])]})])],"derivedFrom":makeQuery(id+"F5.opExtrude","CAP_EDGE",EDGE,{"disambiguationData":[OSD([subQ0])],"isStart":false})});}
            var Q4;
            {var subQ0=sQuery(id+"F0.wireOp",EDGE,"E25.7");var subQ1=sQuery(id+"F0.wireOp",EDGE,"E25.1");var subQ2=sQuery(id+"F0.wireOp",EDGE,"E25.6");var subQ3=sQuery(id+"F0.wireOp",EDGE,"E25.5");var subQ4=sQuery(id+"F0.wireOp",EDGE,"E25.4");var subQ5=sQuery(id+"F0.wireOp",EDGE,"E25.0");var subQ6=sQuery(id+"F0.wireOp",EDGE,"E25.2");var subQ7=sQuery(id+"F0.wireOp",EDGE,"E25.3");Q4=makeQuery(id+"F8.boolean.opBoolean","INTERSECT",EDGE,{"derivedFrom":[makeQuery(id+"F5.boolean.opBoolean","SPLIT",FACE,{"disambiguationData":[TD([makeQuery(id+"F2.opExtrude","SWEPT_FACE",FACE,{"disambiguationData":[OSD([subQ5])]})])],"derivedFrom":makeQuery(id+"F3.boolean.opBoolean","COPY",FACE,{"derivedFrom":makeQuery(id+"F3.opExtrude","CAP_FACE",FACE,{"disambiguationData":[OSD([subQ5,subQ1,subQ6,subQ7,subQ4,subQ3,subQ2,subQ0])],"isStart":false})})}),makeQuery(id+"F8.opExtrude","SWEPT_FACE",FACE,{"disambiguationData":[OSD([sQuery(id+"F7.wireOp",EDGE,"E67")])]})]});}
            var Q5;
            Q5=makeQuery(id+"F8.boolean.opBoolean","INTERSECT",EDGE,{"disambiguationData":[OD(0.0)],"derivedFrom":[makeQuery(id+"F5.opExtrude","SWEPT_FACE",FACE,{"disambiguationData":[OSD([sQuery(id+"F4.wireOp",EDGE,"E30")])]}),makeQuery(id+"F8.opExtrude","SWEPT_FACE",FACE,{"disambiguationData":[OSD([sQuery(id+"F7.wireOp",EDGE,"E67")])]})]});
            fillet(context, id + "F14", {"entities" : qUnion([Q0, Q1, Q2, Q3, Q4, Q5]), "radius" : 3 * mm, "tangentPropagation" : true, "allowEdgeOverflow" : false});
        }
        {
            var Q0;
            Q0=makeQuery(id+"F1.opExtrude","CAP_EDGE",EDGE,{"disambiguationData":[OSD([sQuery(id+"F0.wireOp",EDGE,"E1.bottom")])],"isStart":false});
            fillet(context, id + "F15", {"entities" : qUnion([Q0]), "radius" : 2 * mm, "tangentPropagation" : true, "allowEdgeOverflow" : false});
        }
        {
            var Q0;
            {var subQ0=sQuery(id+"F0.wireOp",EDGE,"E1.bottom");var subQ1=sQuery(id+"F0.wireOp",EDGE,"E1.top");var subQ2=sQuery(id+"F0.wireOp",EDGE,"E1.left");var subQ3=sQuery(id+"F0.wireOp",EDGE,"E1.right");var subQ4=sQuery(id+"F0.wireOp",EDGE,"E4");var subQ5=sQuery(id+"F0.wireOp",EDGE,"E5");var subQ6=sQuery(id+"F0.wireOp",EDGE,"E6");var subQ7=sQuery(id+"F0.wireOp",EDGE,"E7");var subQ8=sQuery(id+"F0.wireOp",EDGE,"E21.filletArc");var subQ9=sQuery(id+"F0.wireOp",EDGE,"E22.filletArc");var subQ10=sQuery(id+"F0.wireOp",EDGE,"E23.filletArc");var subQ11=sQuery(id+"F0.wireOp",EDGE,"E24.filletArc");Q0=makeQuery(id+"F2.boolean.opBoolean","SPLIT",FACE,{"disambiguationData":[TD([makeQuery(id+"F1.opExtrude","SWEPT_FACE",FACE,{"disambiguationData":[OSD([subQ0])]})])],"derivedFrom":makeQuery(id+"F1.opExtrude","CAP_FACE",FACE,{"disambiguationData":[OSD([subQ0,subQ1,subQ2,subQ3,subQ4,subQ5,subQ6,subQ7,subQ8,subQ9,subQ10,subQ11])],"isStart":true})});}
            var sketch = newSketch(context, id + "F16", { "sketchPlane" : qUnion([Q0])});
            skCircle(sketch, "E79.1", {"center": v(34.05, 50.88) * mm, "radius": 4 * mm});
            skCircle(sketch, "E79.2", {"center": v(34.05, 185.88) * mm, "radius": 4 * mm});
            skCircle(sketch, "E79.3", {"center": v(154.05, 185.88) * mm, "radius": 4 * mm});
            skCircle(sketch, "E79.4", {"center": v(154.05, 50.88) * mm, "radius": 4 * mm});
            skLineSegment(sketch, "E80", {"start": v(94.05, 208.38) * mm, "end": v(94.05, 238.38) * mm, "construction": true});
            skCircle(sketch, "E81", {"center": v(94.05, 238.38) * mm, "radius": 6 * mm});
            skArc(sketch, "E82", {"start": v(109.05, 238.38) * mm, "mid": v(94.05, 253.38) * mm, "end": v(79.05, 238.38) * mm});
            skLineSegment(sketch, "E83", {"start": v(79.05, 238.38) * mm, "end": v(79.05, 226.38) * mm});
            skLineSegment(sketch, "E84", {"start": v(109.05, 238.38) * mm, "end": v(109.05, 226.38) * mm});
            skLineSegment(sketch, "E85", {"start": v(79.05, 226.38) * mm, "end": v(61.05, 208.38) * mm});
            skLineSegment(sketch, "E86", {"start": v(109.05, 226.38) * mm, "end": v(127.05, 208.38) * mm});
            skLineSegment(sketch, "E87", {"start": v(174.05, 118.38) * mm, "end": v(14.05, 118.38) * mm, "construction": true});
            skLineSegment(sketch, "E88.MirrorCS", {"start": v(79.05, 10.38) * mm, "end": v(61.05, 28.38) * mm});
            skLineSegment(sketch, "E89.MirrorCS", {"start": v(79.05, -1.62) * mm, "end": v(79.05, 10.38) * mm});
            skArc(sketch, "E90.MirrorCS", {"start": v(109.05, -1.62) * mm, "mid": v(94.05, -16.62) * mm, "end": v(79.05, -1.62) * mm});
            skCircle(sketch, "E91.MirrorC", {"center": v(94.05, -1.62) * mm, "radius": 6 * mm});
            skLineSegment(sketch, "E92.MirrorCS", {"start": v(94.05, 28.38) * mm, "end": v(94.05, -1.62) * mm});
            skLineSegment(sketch, "E93.MirrorCS", {"start": v(109.05, -1.62) * mm, "end": v(109.05, 10.38) * mm});
            skLineSegment(sketch, "E94.MirrorCS", {"start": v(109.05, 10.38) * mm, "end": v(127.05, 28.38) * mm});
            skSolve(sketch);
        }
        {
            var Q0;
            {var subQ3=sQuery(id+"F16.wireOp",EDGE,"E88.MirrorCS");Q0=makeQuery(id+"F16.imprint","IMPRINT",FACE,{"disambiguationData":[TD([[makeQuery(id+"F16.imprint","IMPRINT",EDGE,{"derivedFrom":subQ3}),-1.0]])]});}
            var Q1;
            Q1=makeQuery(id+"F16.imprint","IMPRINT",FACE,{"disambiguationData":[TD([[makeQuery(id+"F16.imprint","IMPRINT",EDGE,{"derivedFrom":sQuery(id+"F16.wireOp",EDGE,"E81")}),-1.0]])]});
            var Q2;
            Q2=makeQuery(id+"F16.imprint","IMPRINT",FACE,{"disambiguationData":[TD([[makeQuery(id+"F16.imprint","IMPRINT",EDGE,{"derivedFrom":sQuery(id+"F16.wireOp",EDGE,"E79.1")}),-1.0]])]});
            var Q3;
            Q3=makeQuery(id+"F2.opExtrude","CAP_FACE",FACE,{"disambiguationData":[OSD([sQuery(id+"F0.wireOp",EDGE,"E12"),sQuery(id+"F0.wireOp",EDGE,"E13"),sQuery(id+"F0.wireOp",EDGE,"E14"),sQuery(id+"F0.wireOp",EDGE,"E15"),sQuery(id+"F0.wireOp",EDGE,"E17.filletArc"),sQuery(id+"F0.wireOp",EDGE,"E18.filletArc"),sQuery(id+"F0.wireOp",EDGE,"E19.filletArc"),sQuery(id+"F0.wireOp",EDGE,"E20.filletArc"),sQuery(id+"F0.wireOp",EDGE,"E25.0"),sQuery(id+"F0.wireOp",EDGE,"E25.1"),sQuery(id+"F0.wireOp",EDGE,"E25.2"),sQuery(id+"F0.wireOp",EDGE,"E25.3"),sQuery(id+"F0.wireOp",EDGE,"E25.4"),sQuery(id+"F0.wireOp",EDGE,"E25.5"),sQuery(id+"F0.wireOp",EDGE,"E25.6"),sQuery(id+"F0.wireOp",EDGE,"E25.7")])],"isStart":false});
            extrude(context, id + "F17", {"entities" : qUnion([Q0, Q1, Q2]), "operationType" : NewBodyOperationType.ADD, "endBound" : BoundingType.UP_TO_SURFACE, "endBoundEntityFace" : qUnion([Q3]), "depth" : 25 * mm});
        }
    });
